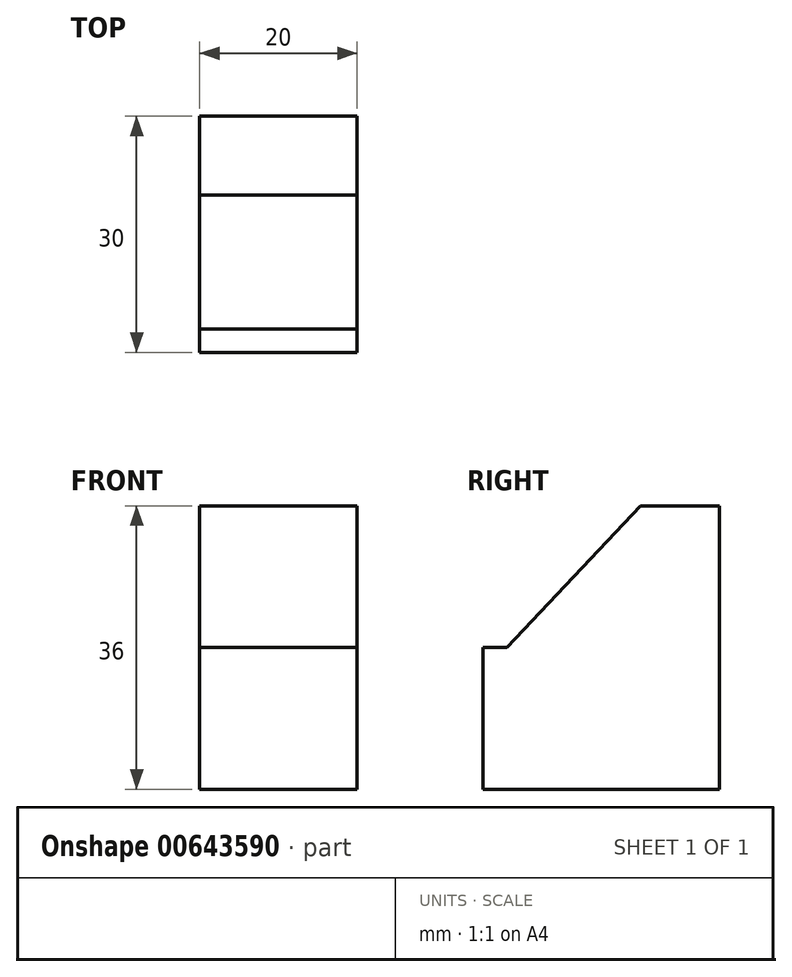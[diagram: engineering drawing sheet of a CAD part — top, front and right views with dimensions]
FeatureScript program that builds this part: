
annotation { "Feature Type Name" : "Feature", "Feature Type Description" : "" }
export const myFeature = defineFeature(function(context is Context, id is Id, definition is map)
    precondition{}
    {
        {
            var Q0;
            Q0=qCreatedBy(makeId("Right.planeOp"),FACE);
            var sketch = newSketch(context, id + "F0", { "sketchPlane" : qUnion([Q0])});
            skLineSegment(sketch, "E0", {"start": v(0, 0) * mm, "end": v(-30, 0) * mm});
            skLineSegment(sketch, "E1", {"start": v(-30, 0) * mm, "end": v(-30, 18) * mm});
            skLineSegment(sketch, "E2", {"start": v(-30, 18) * mm, "end": v(-27, 18) * mm});
            skLineSegment(sketch, "E3", {"start": v(-27, 18) * mm, "end": v(-10, 36) * mm});
            skLineSegment(sketch, "E4", {"start": v(-10, 36) * mm, "end": v(0, 36) * mm});
            skLineSegment(sketch, "E5", {"start": v(0, 36) * mm, "end": v(0, 0) * mm});
            skSolve(sketch);
        }
        {
            var Q0;
            Q0=makeQuery(id+"F0.imprint","IMPRINT",FACE,{"disambiguationData":[TD([[makeQuery(id+"F0.imprint","IMPRINT",EDGE,{"derivedFrom":sQuery(id+"F0.wireOp",EDGE,"E0")}),-1.0]])]});
            extrude(context, id + "F1", {"entities" : qUnion([Q0]), "endBound" : BoundingType.SYMMETRIC, "depth" : 20 * mm, "offsetDistance" : 25 * mm});
        }
    });
